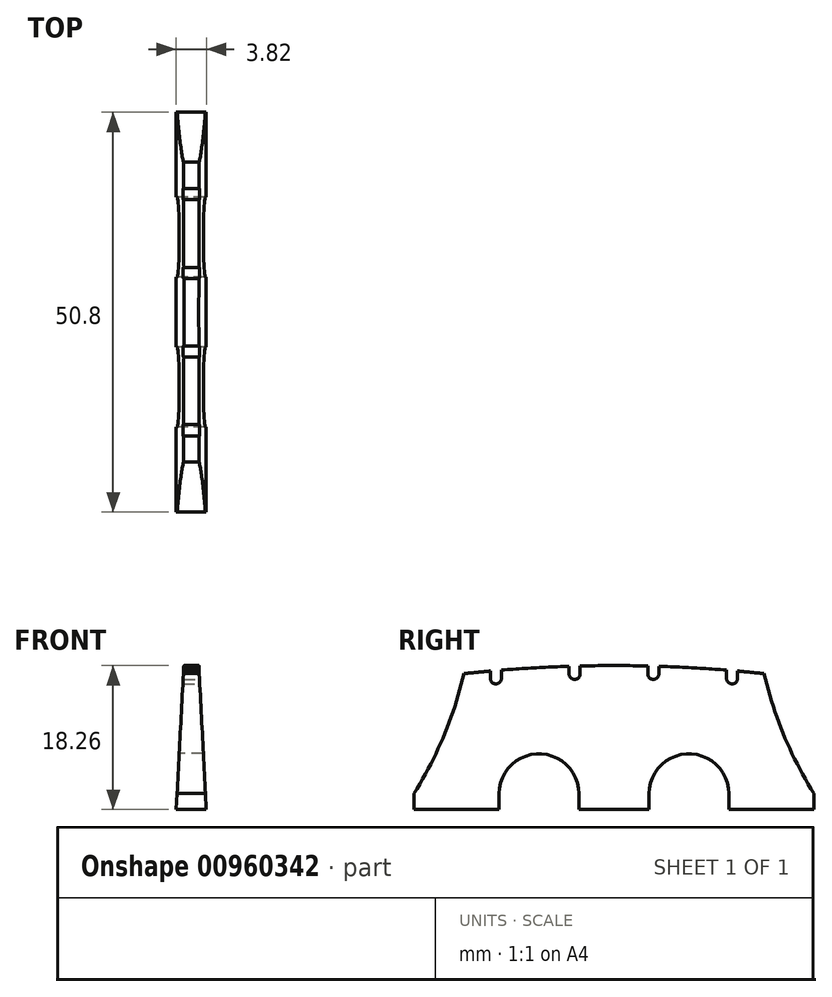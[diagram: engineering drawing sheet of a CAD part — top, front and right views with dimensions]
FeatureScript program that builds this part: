
annotation { "Feature Type Name" : "Feature", "Feature Type Description" : "" }
export const myFeature = defineFeature(function(context is Context, id is Id, definition is map)
    precondition{}
    {
        {
            var Q0;
            Q0=qCreatedBy(makeId("Right.planeOp"),FACE);
            var sketch = newSketch(context, id + "F0", { "sketchPlane" : qUnion([Q0])});
            skArc(sketch, "E0", {"start": v(-25.4, 0) * mm, "mid": v(-21.6, 7.36) * mm, "end": v(-19.05, 15.24) * mm});
            skArc(sketch, "E1", {"start": v(19.05, 15.24) * mm, "mid": v(21.6, 7.36) * mm, "end": v(25.4, 0) * mm});
            skLineSegment(sketch, "E2", {"start": v(-19.05, 15.24) * mm, "end": v(19.05, 15.24) * mm, "construction": true});
            skLineSegment(sketch, "E3", {"start": v(0, 15.24) * mm, "end": v(0, 0) * mm, "construction": true});
            skArc(sketch, "E4", {"start": v(19.05, 15.24) * mm, "mid": v(0, 16.26) * mm, "end": v(-19.05, 15.24) * mm});
            skArc(sketch, "E5", {"start": v(-14.6, 0) * mm, "mid": v(-9.53, 5.08) * mm, "end": v(-4.44, 0) * mm});
            skArc(sketch, "E6", {"start": v(4.45, 0) * mm, "mid": v(9.53, 5.08) * mm, "end": v(14.6, 0) * mm});
            skLineSegment(sketch, "E7", {"start": v(-25.4, 0) * mm, "end": v(-25.4, -2) * mm});
            skLineSegment(sketch, "E8", {"start": v(-25.4, -2) * mm, "end": v(-14.6, -2) * mm});
            skLineSegment(sketch, "E9", {"start": v(-14.6, -2) * mm, "end": v(-14.6, 0) * mm});
            skLineSegment(sketch, "E10", {"start": v(-4.44, 0) * mm, "end": v(-4.44, -2) * mm});
            skLineSegment(sketch, "E11", {"start": v(-4.44, -2) * mm, "end": v(4.44, -2) * mm});
            skLineSegment(sketch, "E12", {"start": v(4.44, -2) * mm, "end": v(4.44, 0) * mm});
            skLineSegment(sketch, "E13", {"start": v(14.6, 0) * mm, "end": v(14.6, -2) * mm});
            skLineSegment(sketch, "E14", {"start": v(14.6, -2) * mm, "end": v(25.4, -2) * mm});
            skLineSegment(sketch, "E15", {"start": v(25.4, -2) * mm, "end": v(25.4, 0) * mm});
            skSolve(sketch);
        }
        {
            var Q0;
            Q0=makeQuery(id+"F0.imprint","IMPRINT",FACE,{"disambiguationData":[TD([[makeQuery(id+"F0.imprint","IMPRINT",EDGE,{"derivedFrom":sQuery(id+"F0.wireOp",EDGE,"E0")}),-1.0]])]});
            extrude(context, id + "F1", {"entities" : qUnion([Q0]), "depth" : 3.8 * mm, "offsetDistance" : 25.4 * mm, "symmetric" : true});
        }
        {
            var Q0;
            Q0=makeQuery(id+"F1.opExtrude","CAP_FACE",FACE,{"disambiguationData":[OSD([sQuery(id+"F0.wireOp",EDGE,"E0"),sQuery(id+"F0.wireOp",EDGE,"E1"),sQuery(id+"F0.wireOp",EDGE,"E4"),sQuery(id+"F0.wireOp",EDGE,"E5"),sQuery(id+"F0.wireOp",EDGE,"E6"),sQuery(id+"F0.wireOp",EDGE,"oACRBz6u-wrlf-bSmT-uHCS-tCXCwqbcEqGS"),sQuery(id+"F0.wireOp",EDGE,"BxzZ67Ve-MDic-4BB6-o1yu-ubHnhybl1myM"),sQuery(id+"F0.wireOp",EDGE,"C25q1kCj-ep9g-jp5U-3cVE-gjTpzy4uoqD4")])],"isStart":false});
            var sketch = newSketch(context, id + "F2", { "sketchPlane" : qUnion([Q0])});
            skArc(sketch, "E16.0", {"start": v(19.3, 14.2) * mm, "mid": v(0, 15.26) * mm, "end": v(-19.3, 14.2) * mm, "construction": true});
            skCircle(sketch, "E17", {"center": v(-15, 14.63) * mm, "radius": 0.7 * mm});
            skCircle(sketch, "E18", {"center": v(-5, 15.2) * mm, "radius": 0.7 * mm});
            skCircle(sketch, "E19", {"center": v(5, 15.2) * mm, "radius": 0.7 * mm});
            skCircle(sketch, "E20", {"center": v(15, 14.63) * mm, "radius": 0.7 * mm});
            skLineSegment(sketch, "E21", {"start": v(-15.7, 14.63) * mm, "end": v(-15.7, 15.57) * mm});
            skLineSegment(sketch, "E22", {"start": v(-14.3, 15.69) * mm, "end": v(-14.3, 14.63) * mm});
            skLineSegment(sketch, "E23", {"start": v(0, 0) * mm, "end": v(0, 16.26) * mm, "construction": true});
            skLineSegment(sketch, "E24", {"start": v(-5.7, 15.2) * mm, "end": v(-5.7, 16.17) * mm});
            skLineSegment(sketch, "E25", {"start": v(-4.3, 16.21) * mm, "end": v(-4.3, 15.2) * mm});
            skLineSegment(sketch, "E26", {"start": v(4.3, 15.2) * mm, "end": v(4.3, 16.21) * mm});
            skLineSegment(sketch, "E27", {"start": v(5.7, 16.17) * mm, "end": v(5.7, 15.2) * mm});
            skLineSegment(sketch, "E28", {"start": v(14.3, 14.63) * mm, "end": v(14.3, 15.69) * mm});
            skLineSegment(sketch, "E29", {"start": v(15.7, 15.57) * mm, "end": v(15.7, 14.63) * mm});
            skSolve(sketch);
        }
        {
            var Q0;
            {var subQ0=sQuery(id+"F2.wireOp",EDGE,"E21");Q0=makeQuery(id+"F2.imprint","IMPRINT",FACE,{"disambiguationData":[TD([[makeQuery(id+"F2.imprint","IMPRINT",EDGE,{"derivedFrom":subQ0}),-1.0]])]});}
            var Q1;
            {var subQ0=sQuery(id+"F2.wireOp",EDGE,"E17");var subQ1=makeQuery(id+"F2.imprint","INTERSECT",VERTEX,{"derivedFrom":[subQ0,sQuery(id+"F2.wireOp",EDGE,"E21")]});Q1=makeQuery(id+"F2.imprint","IMPRINT",FACE,{"disambiguationData":[TD([[makeQuery(id+"F2.imprint","IMPRINT",EDGE,{"disambiguationData":[TD([[subQ1,1.0]])],"derivedFrom":subQ0}),1.0]])]});}
            var Q2;
            {var subQ0=sQuery(id+"F2.wireOp",EDGE,"E24");Q2=makeQuery(id+"F2.imprint","IMPRINT",FACE,{"disambiguationData":[TD([[makeQuery(id+"F2.imprint","IMPRINT",EDGE,{"derivedFrom":subQ0}),-1.0]])]});}
            var Q3;
            {var subQ0=sQuery(id+"F2.wireOp",EDGE,"E18");var subQ1=makeQuery(id+"F2.imprint","INTERSECT",VERTEX,{"derivedFrom":[subQ0,sQuery(id+"F2.wireOp",EDGE,"E24")]});Q3=makeQuery(id+"F2.imprint","IMPRINT",FACE,{"disambiguationData":[TD([[makeQuery(id+"F2.imprint","IMPRINT",EDGE,{"disambiguationData":[TD([[subQ1,1.0]])],"derivedFrom":subQ0}),1.0]])]});}
            var Q4;
            {var subQ0=sQuery(id+"F2.wireOp",EDGE,"E26");Q4=makeQuery(id+"F2.imprint","IMPRINT",FACE,{"disambiguationData":[TD([[makeQuery(id+"F2.imprint","IMPRINT",EDGE,{"derivedFrom":subQ0}),-1.0]])]});}
            var Q5;
            {var subQ0=sQuery(id+"F2.wireOp",EDGE,"E19");var subQ1=makeQuery(id+"F2.imprint","INTERSECT",VERTEX,{"derivedFrom":[subQ0,sQuery(id+"F2.wireOp",EDGE,"E26")]});Q5=makeQuery(id+"F2.imprint","IMPRINT",FACE,{"disambiguationData":[TD([[makeQuery(id+"F2.imprint","IMPRINT",EDGE,{"disambiguationData":[TD([[subQ1,1.0]])],"derivedFrom":subQ0}),1.0]])]});}
            var Q6;
            {var subQ0=sQuery(id+"F2.wireOp",EDGE,"E28");Q6=makeQuery(id+"F2.imprint","IMPRINT",FACE,{"disambiguationData":[TD([[makeQuery(id+"F2.imprint","IMPRINT",EDGE,{"derivedFrom":subQ0}),-1.0]])]});}
            var Q7;
            {var subQ0=sQuery(id+"F2.wireOp",EDGE,"E20");var subQ1=makeQuery(id+"F2.imprint","INTERSECT",VERTEX,{"derivedFrom":[subQ0,sQuery(id+"F2.wireOp",EDGE,"E28")]});Q7=makeQuery(id+"F2.imprint","IMPRINT",FACE,{"disambiguationData":[TD([[makeQuery(id+"F2.imprint","IMPRINT",EDGE,{"disambiguationData":[TD([[subQ1,1.0]])],"derivedFrom":subQ0}),1.0]])]});}
            extrude(context, id + "F3", {"entities" : qUnion([Q0, Q1, Q2, Q3, Q4, Q5, Q6, Q7]), "operationType" : NewBodyOperationType.REMOVE, "endBound" : BoundingType.THROUGH_ALL, "oppositeDirection" : true, "depth" : 25.4 * mm, "offsetDistance" : 25.4 * mm});
        }
        {
            var Q0;
            Q0=qCreatedBy(makeId("Front.planeOp"),FACE);
            var sketch = newSketch(context, id + "F4", { "sketchPlane" : qUnion([Q0])});
            skLineSegment(sketch, "E30", {"start": v(-1.9, -2) * mm, "end": v(0, 34.42) * mm});
            skLineSegment(sketch, "E31", {"start": v(-1.9, -2) * mm, "end": v(-1.9, 34.42) * mm});
            skLineSegment(sketch, "E32", {"start": v(0, 0) * mm, "end": v(0, 16.21) * mm, "construction": true});
            skLineSegment(sketch, "E33", {"start": v(1.9, -2) * mm, "end": v(0, 34.42) * mm});
            skLineSegment(sketch, "E34", {"start": v(1.9, 34.42) * mm, "end": v(1.9, -2) * mm});
            skLineSegment(sketch, "E35", {"start": v(-1.9, 34.42) * mm, "end": v(1.9, 34.42) * mm});
            skPoint(sketch, "E36", {"position": v(-0.95, 16.21) * mm});
            skPoint(sketch, "E37", {"position": v(0.95, 16.21) * mm});
            skSolve(sketch);
        }
        {
            var Q0;
            Q0 = qSketchRegion(id + "F4", true);
            extrude(context, id + "F5", {"entities" : qUnion([Q0]), "operationType" : NewBodyOperationType.REMOVE, "oppositeDirection" : true, "depth" : 50.8 * mm, "offsetDistance" : 25.4 * mm, "symmetric" : true});
        }
    });
